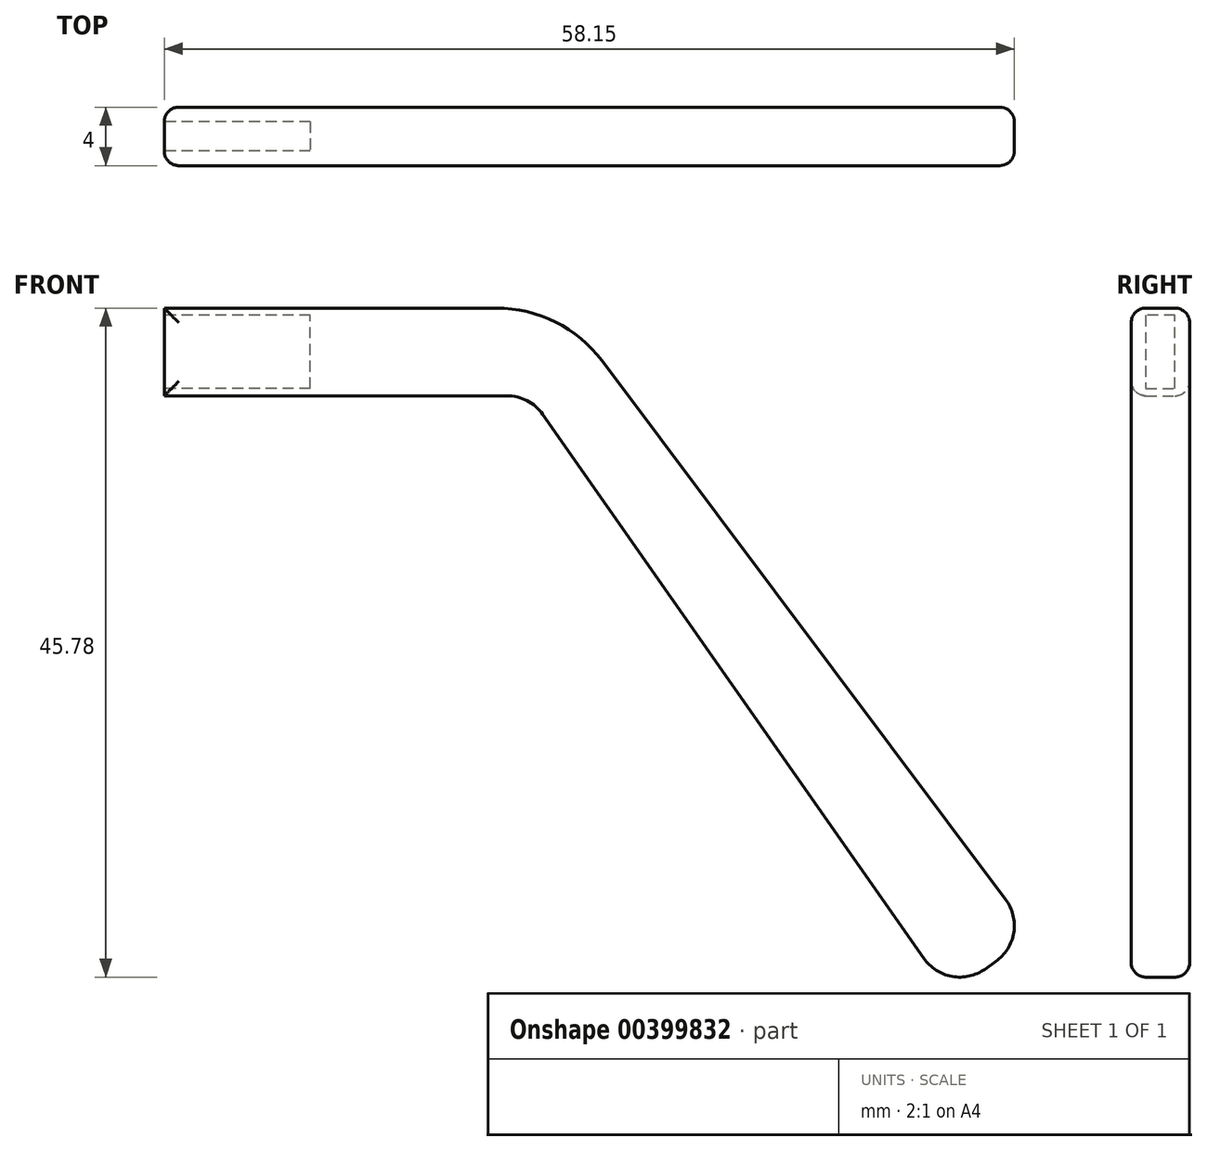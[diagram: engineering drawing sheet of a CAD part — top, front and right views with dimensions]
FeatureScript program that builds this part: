
annotation { "Feature Type Name" : "Feature", "Feature Type Description" : "" }
export const myFeature = defineFeature(function(context is Context, id is Id, definition is map)
    precondition{}
    {
        {
            var Q0;
            Q0=qCreatedBy(makeId("Front.planeOp"),FACE);
            var sketch = newSketch(context, id + "F0", { "sketchPlane" : qUnion([Q0])});
            skLineSegment(sketch, "E0", {"start": v(0, 0) * mm, "end": v(0, -6) * mm});
            skLineSegment(sketch, "E1", {"start": v(0, -6) * mm, "end": v(25, -6) * mm});
            skLineSegment(sketch, "E2", {"start": v(25, -6) * mm, "end": v(53.68, -46.96) * mm});
            skLineSegment(sketch, "E3", {"start": v(53.68, -46.96) * mm, "end": v(59.41, -42.94) * mm});
            skLineSegment(sketch, "E4", {"start": v(0, 0) * mm, "end": v(27.25, 0) * mm});
            skLineSegment(sketch, "E5", {"start": v(27.25, 0) * mm, "end": v(59.41, -42.94) * mm});
            skSolve(sketch);
        }
        {
            var Q0;
            Q0=makeQuery(id+"F0.imprint","IMPRINT",FACE,{"disambiguationData":[TD([[makeQuery(id+"F0.imprint","IMPRINT",EDGE,{"derivedFrom":sQuery(id+"F0.wireOp",EDGE,"E0")}),1.0]])]});
            extrude(context, id + "F1", {"entities" : qUnion([Q0]), "endBound" : BoundingType.SYMMETRIC, "depth" : 4 * mm});
        }
        {
            var Q0;
            Q0=makeQuery(id+"F1.opExtrude","SWEPT_EDGE",EDGE,{"disambiguationData":[OSD([sQuery(id+"F0.wireOp",EDGE,"E1"),sQuery(id+"F0.wireOp",EDGE,"E2")])]});
            var Q1;
            Q1=makeQuery(id+"F1.opExtrude","SWEPT_EDGE",EDGE,{"disambiguationData":[OSD([sQuery(id+"F0.wireOp",EDGE,"E2"),sQuery(id+"F0.wireOp",EDGE,"E3")])]});
            var Q2;
            Q2=makeQuery(id+"F1.opExtrude","SWEPT_EDGE",EDGE,{"disambiguationData":[OSD([sQuery(id+"F0.wireOp",EDGE,"E3"),sQuery(id+"F0.wireOp",EDGE,"E5")])]});
            fillet(context, id + "F2", {"entities" : qUnion([Q0, Q1, Q2]), "radius" : 3 * mm, "tangentPropagation" : true, "allowEdgeOverflow" : false});
        }
        {
            var Q0;
            Q0=makeQuery(id+"F1.opExtrude","SWEPT_EDGE",EDGE,{"disambiguationData":[OSD([sQuery(id+"F0.wireOp",EDGE,"E4"),sQuery(id+"F0.wireOp",EDGE,"E5")])]});
            fillet(context, id + "F3", {"entities" : qUnion([Q0]), "radius" : 9 * mm, "tangentPropagation" : true, "allowEdgeOverflow" : false});
        }
        {
            var Q0;
            Q0=makeQuery(id+"F1.opExtrude","SWEPT_FACE",FACE,{"disambiguationData":[OSD([sQuery(id+"F0.wireOp",EDGE,"E0")])]});
            var sketch = newSketch(context, id + "F4", { "sketchPlane" : qUnion([Q0])});
            skLineSegment(sketch, "E6", {"start": v(-2, 0) * mm, "end": v(-1, 0) * mm, "construction": true});
            skLineSegment(sketch, "E7", {"start": v(-1, 0) * mm, "end": v(-1, -0.5) * mm, "construction": true});
            skLineSegment(sketch, "E8", {"start": v(-1, -0.5) * mm, "end": v(1, -0.5) * mm});
            skLineSegment(sketch, "E9", {"start": v(1, -0.5) * mm, "end": v(1, -5.5) * mm});
            skLineSegment(sketch, "E10", {"start": v(1, -5.5) * mm, "end": v(-1, -5.5) * mm});
            skLineSegment(sketch, "E11", {"start": v(-1, -5.5) * mm, "end": v(-1, -0.5) * mm});
            skSolve(sketch);
        }
        {
            var Q0;
            Q0=makeQuery(id+"F4.imprint","IMPRINT",FACE,{"disambiguationData":[TD([[makeQuery(id+"F4.imprint","IMPRINT",EDGE,{"derivedFrom":sQuery(id+"F4.wireOp",EDGE,"E8")}),-1.0]])]});
            extrude(context, id + "F5", {"entities" : qUnion([Q0]), "operationType" : NewBodyOperationType.REMOVE, "oppositeDirection" : true, "depth" : 10 * mm});
        }
        {
            var Q0;
            Q0=makeQuery(id+"F1.opExtrude","CAP_FACE",FACE,{"disambiguationData":[OSD([sQuery(id+"F0.wireOp",EDGE,"E0"),sQuery(id+"F0.wireOp",EDGE,"E1"),sQuery(id+"F0.wireOp",EDGE,"E2"),sQuery(id+"F0.wireOp",EDGE,"E3"),sQuery(id+"F0.wireOp",EDGE,"E4"),sQuery(id+"F0.wireOp",EDGE,"E5")])],"isStart":false});
            var Q1;
            Q1=makeQuery(id+"F1.opExtrude","CAP_FACE",FACE,{"disambiguationData":[OSD([sQuery(id+"F0.wireOp",EDGE,"E0"),sQuery(id+"F0.wireOp",EDGE,"E1"),sQuery(id+"F0.wireOp",EDGE,"E2"),sQuery(id+"F0.wireOp",EDGE,"E3"),sQuery(id+"F0.wireOp",EDGE,"E4"),sQuery(id+"F0.wireOp",EDGE,"E5")])],"isStart":true});
            fillet(context, id + "F6", {"entities" : qUnion([Q0, Q1]), "radius" : 1 * mm, "tangentPropagation" : true, "allowEdgeOverflow" : false});
        }
    });
